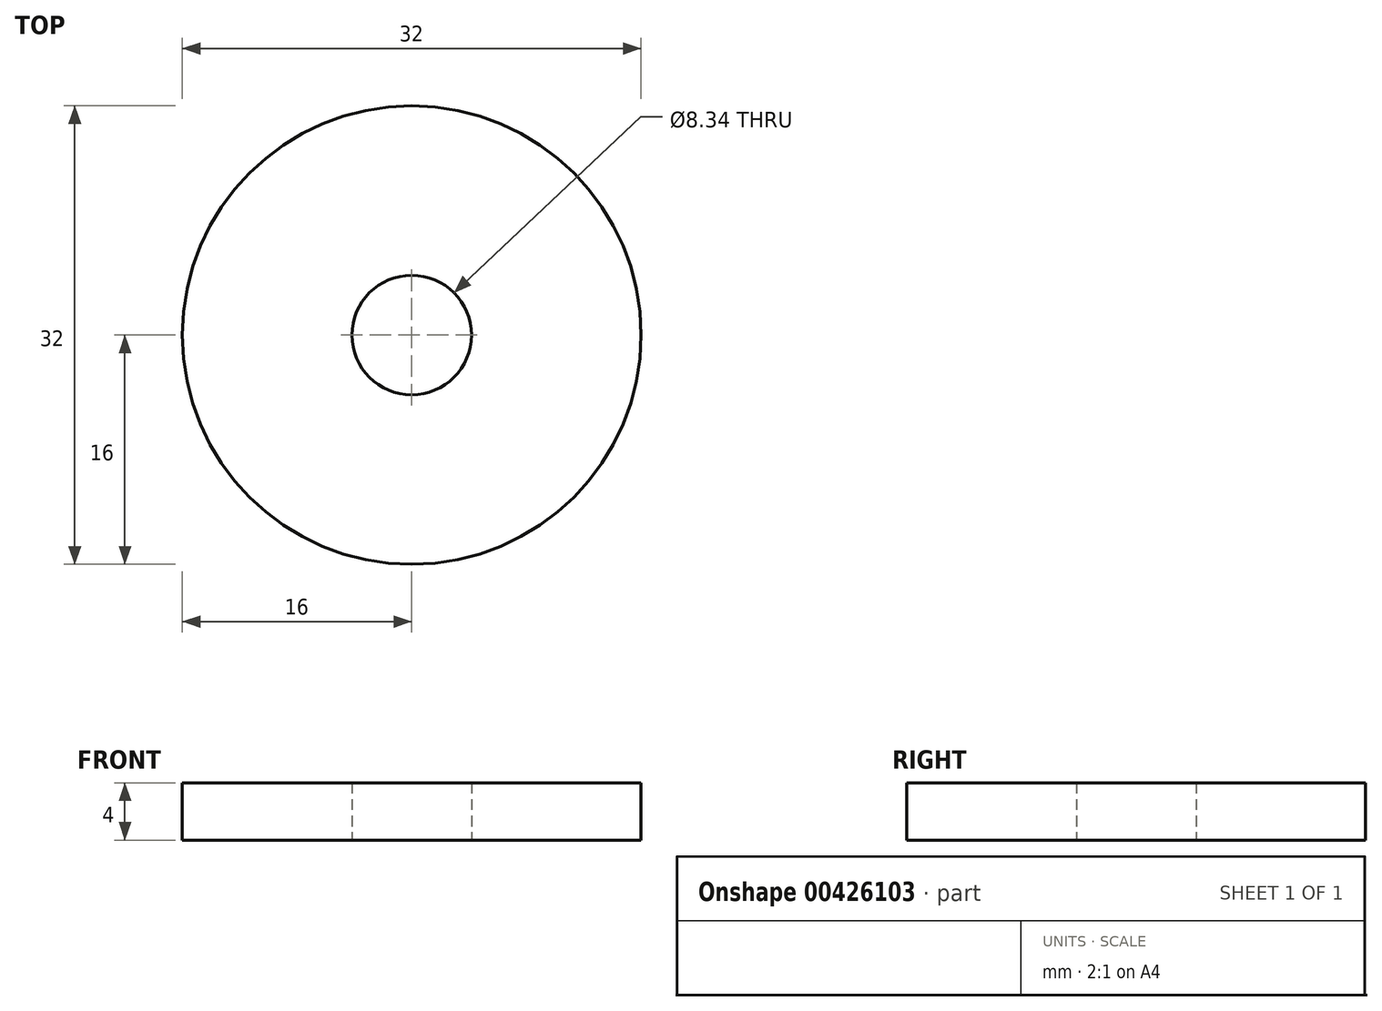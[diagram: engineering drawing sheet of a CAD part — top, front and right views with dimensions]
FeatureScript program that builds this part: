
annotation { "Feature Type Name" : "Feature", "Feature Type Description" : "" }
export const myFeature = defineFeature(function(context is Context, id is Id, definition is map)
    precondition{}
    {
        {
            var Q0;
            Q0=qCreatedBy(makeId("Top.planeOp"),FACE);
            var sketch = newSketch(context, id + "F0", { "sketchPlane" : qUnion([Q0])});
            skCircle(sketch, "E0", {"center": v(0, 0) * mm, "radius": 16 * mm});
            skCircle(sketch, "E1", {"center": v(0, 0) * mm, "radius": 4.17 * mm});
            skSolve(sketch);
        }
        {
            var Q0;
            Q0=makeQuery(id+"F0.imprint","IMPRINT",FACE,{"disambiguationData":[TD([[makeQuery(id+"F0.imprint","IMPRINT",EDGE,{"derivedFrom":sQuery(id+"F0.wireOp",EDGE,"E0")}),1.0]])]});
            extrude(context, id + "F1", {"entities" : qUnion([Q0]), "depth" : 4 * mm});
        }
    });
